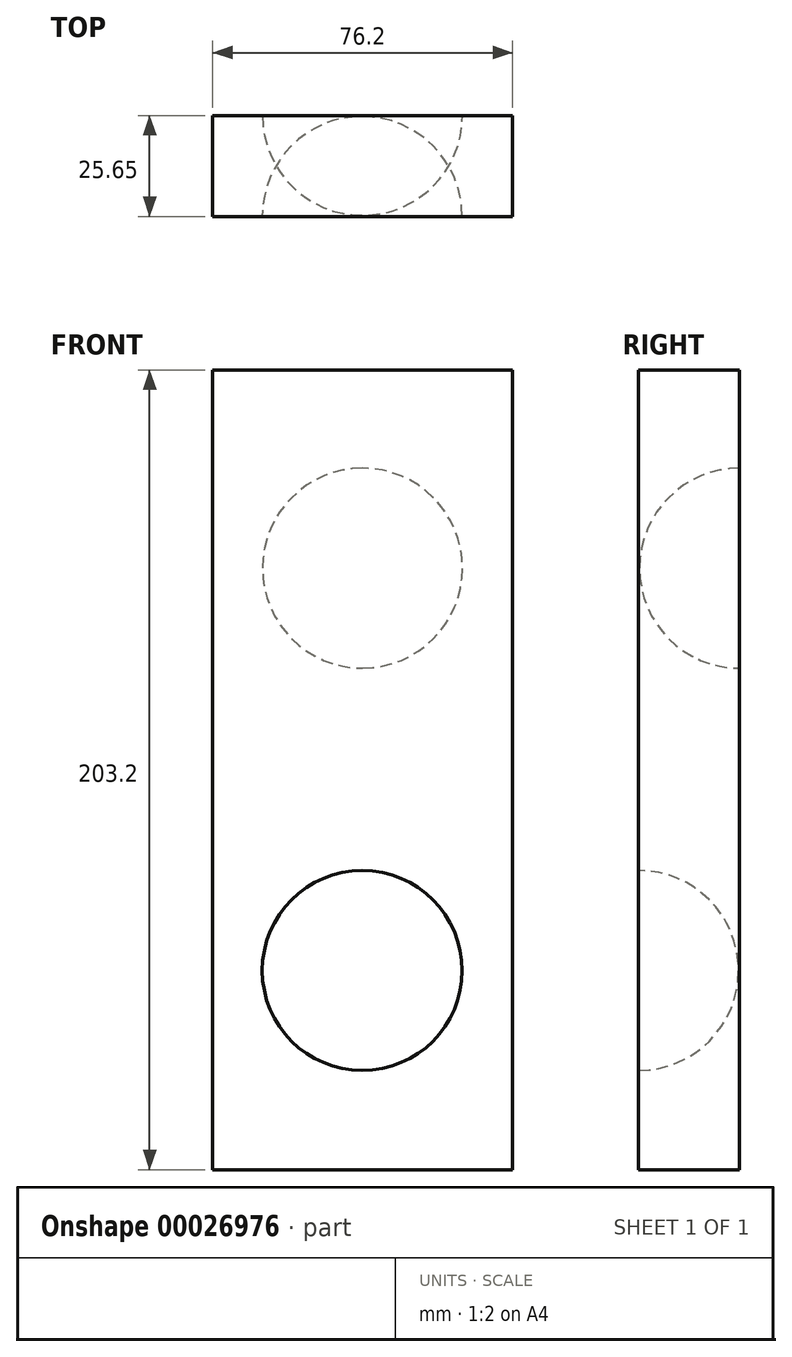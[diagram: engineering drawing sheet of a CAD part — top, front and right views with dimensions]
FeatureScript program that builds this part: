
annotation { "Feature Type Name" : "Feature", "Feature Type Description" : "" }
export const myFeature = defineFeature(function(context is Context, id is Id, definition is map)
    precondition{}
    {
        {
            var Q0;
            Q0=qCreatedBy(makeId("Front.planeOp"),FACE);
            var sketch = newSketch(context, id + "F0", { "sketchPlane" : qUnion([Q0])});
            skLineSegment(sketch, "E0.bottom", {"start": v(32.6, -94.42) * mm, "end": v(-43.6, -94.42) * mm});
            skLineSegment(sketch, "E0.top", {"start": v(32.6, 108.78) * mm, "end": v(-43.6, 108.78) * mm});
            skLineSegment(sketch, "E0.left", {"start": v(32.6, -94.42) * mm, "end": v(32.6, 108.78) * mm});
            skLineSegment(sketch, "E0.right", {"start": v(-43.6, -94.42) * mm, "end": v(-43.6, 108.78) * mm});
            skLineSegment(sketch, "E1", {"start": v(-5.5, -18.22) * mm, "end": v(-5.5, -69.02) * mm});
            skArc(sketch, "E2", {"start": v(-5.5, -69.02) * mm, "mid": v(19.9, -43.62) * mm, "end": v(-5.5, -18.22) * mm});
            skPoint(sketch, "E3.orphan", {"position": v(-5.5, 7.18) * mm});
            skPoint(sketch, "E4.trimOffspring.end.orphan", {"position": v(32.6, -43.62) * mm});
            skPoint(sketch, "E5.start.orphan", {"position": v(-43.6, -43.62) * mm});
            skPoint(sketch, "E6.orphan", {"position": v(-5.5, -94.42) * mm});
            skLineSegment(sketch, "E7", {"start": v(-5.5, 32.74) * mm, "end": v(-5.5, 83.21) * mm});
            skArc(sketch, "E8", {"start": v(-5.5, 32.74) * mm, "mid": v(19.74, 57.98) * mm, "end": v(-5.5, 83.21) * mm});
            skPoint(sketch, "E9.orphan", {"position": v(-5.5, 108.78) * mm});
            skPoint(sketch, "E10.orphan", {"position": v(-43.6, 57.98) * mm});
            skPoint(sketch, "E11.end.orphan", {"position": v(32.6, 57.98) * mm});
            skPoint(sketch, "E12.orphan", {"position": v(32.6, 108.78) * mm});
            skPoint(sketch, "E13.orphan", {"position": v(-43.6, 7.18) * mm});
            skPoint(sketch, "E14.orphan", {"position": v(-43.6, -94.42) * mm});
            skPoint(sketch, "E15.left.end.orphan", {"position": v(32.6, 7.18) * mm});
            skSolve(sketch);
        }
        {
            var Q0;
            Q0 = qSketchRegion(id + "F0", true);
            var Q1;
            Q1=makeQuery(id+"F0.imprint","IMPRINT",FACE,{"disambiguationData":[TD([[makeQuery(id+"F0.imprint","IMPRINT",EDGE,{"derivedFrom":sQuery(id+"F0.wireOp",EDGE,"E7")}),-1.0]])]});
            var Q2;
            Q2=makeQuery(id+"F0.imprint","IMPRINT",FACE,{"disambiguationData":[TD([[makeQuery(id+"F0.imprint","IMPRINT",EDGE,{"derivedFrom":sQuery(id+"F0.wireOp",EDGE,"E1")}),1.0]])]});
            extrude(context, id + "F1", {"entities" : qUnion([Q0, Q1, Q2]), "oppositeDirection" : true, "depth" : 25.65 * mm});
        }
        {
            var Q0;
            Q0=qCreatedBy(makeId("Front.planeOp"),FACE);
            var sketch = newSketch(context, id + "F2", { "sketchPlane" : qUnion([Q0])});
            skLineSegment(sketch, "E16", {"start": v(-5.6, -18.42) * mm, "end": v(-5.6, -69.22) * mm});
            skArc(sketch, "E17", {"start": v(-5.6, -69.22) * mm, "mid": v(19.8, -43.82) * mm, "end": v(-5.6, -18.42) * mm});
            skLineSegment(sketch, "E18", {"start": v(-5.55, 83.8) * mm, "end": v(-5.55, 33) * mm});
            skArc(sketch, "E19", {"start": v(-5.55, 33) * mm, "mid": v(19.85, 58.4) * mm, "end": v(-5.55, 83.8) * mm});
            skSolve(sketch);
        }
        {
            var Q0;
            Q0=makeQuery(id+"F2.imprint","IMPRINT",FACE,{"disambiguationData":[TD([[makeQuery(id+"F2.imprint","IMPRINT",EDGE,{"derivedFrom":sQuery(id+"F2.wireOp",EDGE,"E16")}),1.0]])]});
            var Q1;
            Q1=sQuery(id+"F2.wireOp",EDGE,"E16");
            revolve(context, id + "F3", {"operationType" : NewBodyOperationType.REMOVE, "entities" : qUnion([Q0]), "axis" : qUnion([Q1]), "revolveType" : RevolveType.FULL, "oppositeDirection" : true});
        }
        {
            var Q0;
            Q0=qCreatedBy(makeId("Front.planeOp"),FACE);
            cPlane(context, id + "F4", {"entities" : qUnion([Q0]), "cplaneType" : CPlaneType.OFFSET, "offset" : 25.65 * mm, "oppositeDirection" : true, "width" : 152.4 * mm, "height" : 152.4 * mm});
        }
        {
            var Q0;
            Q0=qCreatedBy(id+"F4.planeOp",FACE);
            var sketch = newSketch(context, id + "F5", { "sketchPlane" : qUnion([Q0])});
            skLineSegment(sketch, "E20", {"start": v(-5.54, 33) * mm, "end": v(-5.54, 83.8) * mm});
            skArc(sketch, "E21", {"start": v(-5.54, 33) * mm, "mid": v(19.86, 58.4) * mm, "end": v(-5.54, 83.8) * mm});
            skSolve(sketch);
        }
        {
            var Q0;
            Q0 = qSketchRegion(id + "F5", true);
            var Q1;
            Q1=sQuery(id+"F5.wireOp",EDGE,"E20");
            revolve(context, id + "F6", {"operationType" : NewBodyOperationType.REMOVE, "entities" : qUnion([Q0]), "axis" : qUnion([Q1]), "revolveType" : RevolveType.ONE_DIRECTION, "oppositeDirection" : true, "angle" : 180 * degree});
        }
    });
